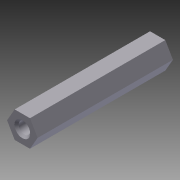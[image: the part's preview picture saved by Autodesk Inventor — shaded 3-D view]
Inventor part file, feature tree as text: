
AUTODESK INVENTOR PART (.ipt)
format: ipt  version: 2014 SP2 (Build 180246200, 246)  size: 132,608 bytes
history: native  units: in
note: dims shown in document units (in); Inventor stores cm internally (conversion verified against a paired STEP export)
features: extrude x3, sketch x3, other x1, mirror x1, imported_body x1
ambient origin geometry x8: Origin, YZ Plane, XZ Plane, XY Plane, X Axis, Y Axis, Z Axis, Center Point
bodies: Solid1 (feature_tree)
feature tree (9):
  other  "1 Inch Standoff.sat1"
  extrude  "Extrusion1"  Depth=0.25in TaperAngle=0.0deg
  extrude  "Extrusion2"  [1 undecoded]
  extrude  "Extrusion3"  [1 undecoded]
  mirror  "Mirror1"
  imported_body  "Base1"
  sketch  "Sketch1"  dims[d0=0.3937in d1=0.0in d2=0.25in d3=0.0in]
  sketch  "Sketch2"  dims[d4=0.25in d5=0.0in]
  sketch  "Sketch3"
note: 2 required parameter values undecoded (feature->parameter linkage not recoverable at this tier; creation-order binding heuristic only, values carry confidence <= 0.55)
